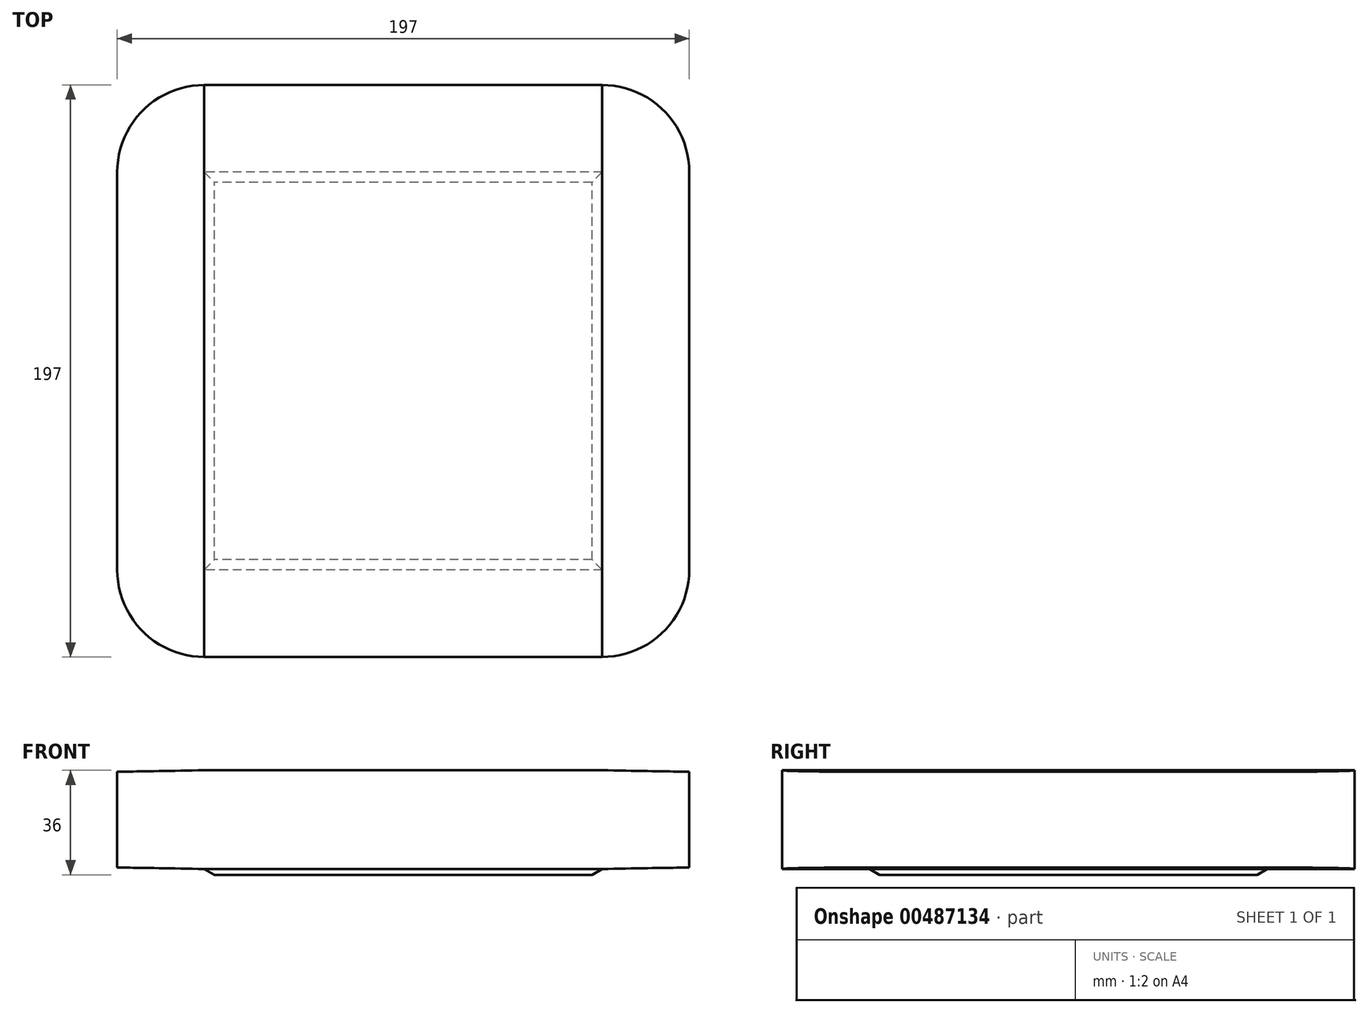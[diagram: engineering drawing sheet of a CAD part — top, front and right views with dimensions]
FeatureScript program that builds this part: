
annotation { "Feature Type Name" : "Feature", "Feature Type Description" : "" }
export const myFeature = defineFeature(function(context is Context, id is Id, definition is map)
    precondition{}
    {
        {
            var Q0;
            Q0=qCreatedBy(makeId("Top.planeOp"),FACE);
            var sketch = newSketch(context, id + "F0", { "sketchPlane" : qUnion([Q0])});
            skLineSegment(sketch, "E0.bottom", {"start": v(0, 0) * mm, "end": v(197, 0) * mm});
            skLineSegment(sketch, "E0.top", {"start": v(0, -197) * mm, "end": v(197, -197) * mm});
            skLineSegment(sketch, "E0.left", {"start": v(0, 0) * mm, "end": v(0, -197) * mm});
            skLineSegment(sketch, "E0.right", {"start": v(197, 0) * mm, "end": v(197, -197) * mm});
            skSolve(sketch);
        }
        {
            var Q0;
            Q0=qSketchRegion(id+"F0",true);
            extrude(context, id + "F1", {"entities" : qUnion([Q0]), "depth" : 34 * mm});
        }
        {
            var Q0;
            Q0=makeQuery(id+"F1.opExtrude","SWEPT_EDGE",EDGE,{"disambiguationData":[OSD([sQuery(id+"F0.wireOp",EDGE,"E0.top"),sQuery(id+"F0.wireOp",EDGE,"E0.right")])]});
            var Q1;
            Q1=makeQuery(id+"F1.opExtrude","SWEPT_EDGE",EDGE,{"disambiguationData":[OSD([sQuery(id+"F0.wireOp",EDGE,"E0.bottom"),sQuery(id+"F0.wireOp",EDGE,"E0.right")])]});
            var Q2;
            Q2=makeQuery(id+"F1.opExtrude","SWEPT_EDGE",EDGE,{"disambiguationData":[OSD([sQuery(id+"F0.wireOp",EDGE,"E0.bottom"),sQuery(id+"F0.wireOp",EDGE,"E0.left")])]});
            var Q3;
            Q3=makeQuery(id+"F1.opExtrude","SWEPT_EDGE",EDGE,{"disambiguationData":[OSD([sQuery(id+"F0.wireOp",EDGE,"E0.top"),sQuery(id+"F0.wireOp",EDGE,"E0.left")])]});
            fillet(context, id + "F2", {"entities" : qUnion([Q0, Q1, Q2, Q3]), "radius" : 30 * mm, "tangentPropagation" : true, "allowEdgeOverflow" : false});
        }
        {
            var Q0;
            Q0=qCreatedBy(makeId("Front.planeOp"),FACE);
            cPlane(context, id + "F3", {"entities" : qUnion([Q0]), "cplaneType" : CPlaneType.OFFSET, "offset" : 197 * mm, "width" : 150 * mm, "height" : 150 * mm});
        }
        {
            var Q0;
            Q0=qCreatedBy(id+"F3.planeOp",FACE);
            var sketch = newSketch(context, id + "F4", { "sketchPlane" : qUnion([Q0])});
            skLineSegment(sketch, "E1", {"start": v(167, 34) * mm, "end": v(197, 34) * mm});
            skLineSegment(sketch, "E2", {"start": v(167, 34) * mm, "end": v(197, 33.48) * mm});
            skLineSegment(sketch, "E3", {"start": v(197, 34) * mm, "end": v(197, 33.48) * mm});
            skLineSegment(sketch, "E4", {"start": v(0, 0) * mm, "end": v(197, 0) * mm});
            skLineSegment(sketch, "E5", {"start": v(98.5, 0) * mm, "end": v(98.5, 31) * mm});
            skLineSegment(sketch, "E6", {"start": v(98.5, 15.5) * mm, "end": v(74.04, 15.5) * mm});
            skLineSegment(sketch, "E7.MirrorCS", {"start": v(197, 0) * mm, "end": v(197, 0.52) * mm});
            skLineSegment(sketch, "E8.MirrorCS", {"start": v(167, 0) * mm, "end": v(197, 0) * mm});
            skLineSegment(sketch, "E9.MirrorCS", {"start": v(167, 0) * mm, "end": v(197, 0.52) * mm});
            skLineSegment(sketch, "E10", {"start": v(197, 0) * mm, "end": v(167, 0) * mm});
            skLineSegment(sketch, "E11.MirrorCS", {"start": v(0, 0) * mm, "end": v(0, 0.52) * mm});
            skLineSegment(sketch, "E12.MirrorCS", {"start": v(0, 34) * mm, "end": v(0, 33.48) * mm});
            skLineSegment(sketch, "E13.MirrorCS", {"start": v(30, 34) * mm, "end": v(0, 34) * mm});
            skLineSegment(sketch, "E14.MirrorCS", {"start": v(30, 0) * mm, "end": v(0, 0) * mm});
            skLineSegment(sketch, "E15.MirrorCS", {"start": v(0, 0) * mm, "end": v(30, 0) * mm});
            skLineSegment(sketch, "E16.MirrorCS", {"start": v(30, 0) * mm, "end": v(0, 0.52) * mm});
            skLineSegment(sketch, "E17.MirrorCS", {"start": v(30, 3) * mm, "end": v(30, 34) * mm});
            skLineSegment(sketch, "E18.MirrorCS", {"start": v(30, 34) * mm, "end": v(0, 33.48) * mm});
            skSolve(sketch);
        }
        {
            var Q0;
            Q0=qSketchRegion(id+"F4",true);
            extrude(context, id + "F5", {"entities" : qUnion([Q0]), "operationType" : NewBodyOperationType.REMOVE, "oppositeDirection" : true, "depth" : 197 * mm});
        }
        {
            var Q0;
            Q0=qCreatedBy(makeId("Top.planeOp"),FACE);
            var sketch = newSketch(context, id + "F6", { "sketchPlane" : qUnion([Q0])});
            skLineSegment(sketch, "E19", {"start": v(0, 0) * mm, "end": v(98.5, 0) * mm});
            skLineSegment(sketch, "E20", {"start": v(98.5, 0) * mm, "end": v(98.5, -98.5) * mm});
            skLineSegment(sketch, "E21.bottom", {"start": v(167, -167) * mm, "end": v(30, -167) * mm});
            skLineSegment(sketch, "E21.top", {"start": v(167, -30) * mm, "end": v(30, -30) * mm});
            skLineSegment(sketch, "E21.left", {"start": v(167, -167) * mm, "end": v(167, -30) * mm});
            skLineSegment(sketch, "E21.right", {"start": v(30, -167) * mm, "end": v(30, -30) * mm});
            skPoint(sketch, "E21.middle", {"position": v(98.5, -98.5) * mm});
            skSolve(sketch);
        }
        {
            var Q0;
            Q0=qCreatedBy(makeId("Top.planeOp"),FACE);
            cPlane(context, id + "F7", {"entities" : qUnion([Q0]), "cplaneType" : CPlaneType.OFFSET, "offset" : 2 * mm, "oppositeDirection" : true, "width" : 150 * mm, "height" : 150 * mm});
        }
        {
            var Q0;
            Q0=qCreatedBy(id+"F7.planeOp",FACE);
            var sketch = newSketch(context, id + "F8", { "sketchPlane" : qUnion([Q0])});
            skLineSegment(sketch, "E22", {"start": v(0, 0) * mm, "end": v(98.5, 0) * mm});
            skLineSegment(sketch, "E23", {"start": v(98.5, 0) * mm, "end": v(98.5, -98.5) * mm});
            skLineSegment(sketch, "E24.bottom", {"start": v(163.5, -163.5) * mm, "end": v(33.5, -163.5) * mm});
            skLineSegment(sketch, "E24.top", {"start": v(163.5, -33.5) * mm, "end": v(33.5, -33.5) * mm});
            skLineSegment(sketch, "E24.left", {"start": v(163.5, -163.5) * mm, "end": v(163.5, -33.5) * mm});
            skLineSegment(sketch, "E24.right", {"start": v(33.5, -163.5) * mm, "end": v(33.5, -33.5) * mm});
            skPoint(sketch, "E24.middle", {"position": v(98.5, -98.5) * mm});
            skSolve(sketch);
        }
        {
            var Q1;
            Q1=makeQuery(id+"F6.imprint","IMPRINT",FACE,{"disambiguationData":[TD([[makeQuery(id+"F6.imprint","IMPRINT",EDGE,{"derivedFrom":sQuery(id+"F6.wireOp",EDGE,"E21.bottom")}),-1.0]])]});
            var Q2;
            Q2=makeQuery(id+"F8.imprint","IMPRINT",FACE,{"disambiguationData":[TD([[makeQuery(id+"F8.imprint","IMPRINT",EDGE,{"derivedFrom":sQuery(id+"F8.wireOp",EDGE,"E24.bottom")}),-1.0]])]});
            loft(context, id + "F9", {"sheetProfilesArray" : [{ "sheetProfileEntities" : qUnion([Q1]) }, { "sheetProfileEntities" : qUnion([Q2]) }]});
        }
    });
